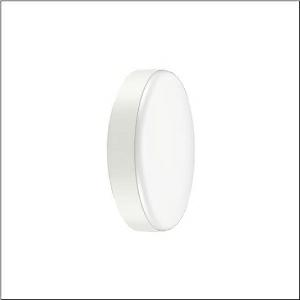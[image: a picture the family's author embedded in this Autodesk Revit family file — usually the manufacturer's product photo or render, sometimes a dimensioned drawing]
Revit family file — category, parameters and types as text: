
# Revit family: round_31_51wc10mb34a
name_source: partatom
category: Lighting Fixtures
units: mm (PartAtom-declared; Revit-internal decimal feet)

## family parameters
Cut with Voids When Loaded = No
Host = Face
Light Source = No
Part Type = Normal
Room Calculation Point = No
Round Connector Dimension = Use Diameter
Shared = No

## types (1)
- --- (1 x LED, 4250 lm, 34 W, 3000K)
    Apparent Load = 34 VA
    CIE Flux Codes = 44 75 94 94 100
    Color Rendering = 80
    Color Temperature = 3000K
    Default Elevation = 1800 mm
    Description = Round 31, wall and ceiling luminaire, primary optical cover: cover, of PC, opal, light emission: direct distribution, primary light characteristic: symmetric, installation type: surface-mounted, LED, rated luminous flux: 4.250lm, luminous efficacy: 125lm/W, light colour: 830, colour temperature: 3000K, control gear: ON/OFF Multilumen, with terminal, 3-pole, max. 2.5mm², mains connection: 220..240V, AC, 50/60Hz, rated input power: 34W, luminaire housing, of PC, traffic white (RAL 9016), diameter: 480mm, protection rating (complete): IP65, insulation class (complete): insulation class II (safety insulation), certification: CE, impact resistance: IK10, permissible operating ambient temperature: -20..+40°C, permissible storage temperature: -20..+60°C, packaging unit: 1 piece
    Height = 97 mm
    Lamp = 1 x LED
    Lamp Light Flux = 4250 lm
    Lamp Power = 34 W
    Lamp count = 1
    Length = 480 mm
    Luminous efficacy = 125 lm/W
    Manufacturer = Siteco
    ModVariant = No
    Model = 51WC10MB34A
    Mounting Place = Ceiling
    Mounting Type = Surface mounted
    Number of Poles = 1
    OnlyDefault = Yes
    Power Factor = 1
    Product Name = Round 31
    Product group = wall and ceiling luminaire | ceiling mounted
    ProductGroupID = 305
    Protection Class = Protection class II
    Protection Degree = IP 65
    RLX_Detail_Level = 1
    RLX_Emergency_Light_Flux = 0 lm
    RLX_Emergency_Type = 0
    RLX_Emergency_Type_DB = No
    RlxData = <blob elided: 42761 chars, md5=0f4aec04>
    Socket = socket
    Standby Power = 0 W
    System Light Flux = 4250 lm
    System Power = 34 W
    Type Comments = factory setting: luminous flux: 100 % | (ON | ON)
    Type Image = l_1007188.jpg
    URL = http://relux.com
    VarID = @adj_172337
    Voltage = 0 V
    Weight = 0.00 kg
    Width = 0 mm  [stored 0 ft]

note: [stored X ft] marks values corroborated as IEEE doubles in the binary element streams (Revit-internal decimal feet)

## geometry (parser evidence)
native form markers: Blend x4, Sweep x13
no freeform markers — native parametric forms only
